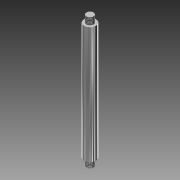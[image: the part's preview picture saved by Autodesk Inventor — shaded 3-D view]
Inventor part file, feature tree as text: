
AUTODESK INVENTOR PART (.ipt)
format: ipt  version: 2012 (Build 160160000, 160)  size: 80,384 bytes
history: native  units: mm
features: extrude x3, sketch x3, thread x2
ambient origin geometry x8: Origin, YZ Plane, XZ Plane, XY Plane, X Axis, Y Axis, Z Axis, Center Point
bodies: Solid1 (feature_tree)
feature tree (8):
  extrude  "Extrusion1"  Depth=50.0mm TaperAngle=0.0deg
  extrude  "Extrusion2"  Depth=3.0mm TaperAngle=0.0deg
  thread  "Thread1"  [1 undecoded]
  extrude  "Extrusion3"  Depth=3.0mm TaperAngle=0.0deg
  thread  "Thread2"  [1 undecoded]
  sketch  "Sketch1"  dims[d0=5.0mm d1=50.0mm d2=0.0mm]
  sketch  "Sketch2"  dims[d3=3.0mm d4=3.0mm d5=0.0mm d6=10.0mm d7=0.0mm]
  sketch  "Sketch3"  dims[d8=3.0mm d9=3.0mm d10=0.0mm d11=10.0mm d12=0.0mm]
note: 2 required parameter values undecoded (feature->parameter linkage not recoverable at this tier; creation-order binding heuristic only, values carry confidence <= 0.55)
